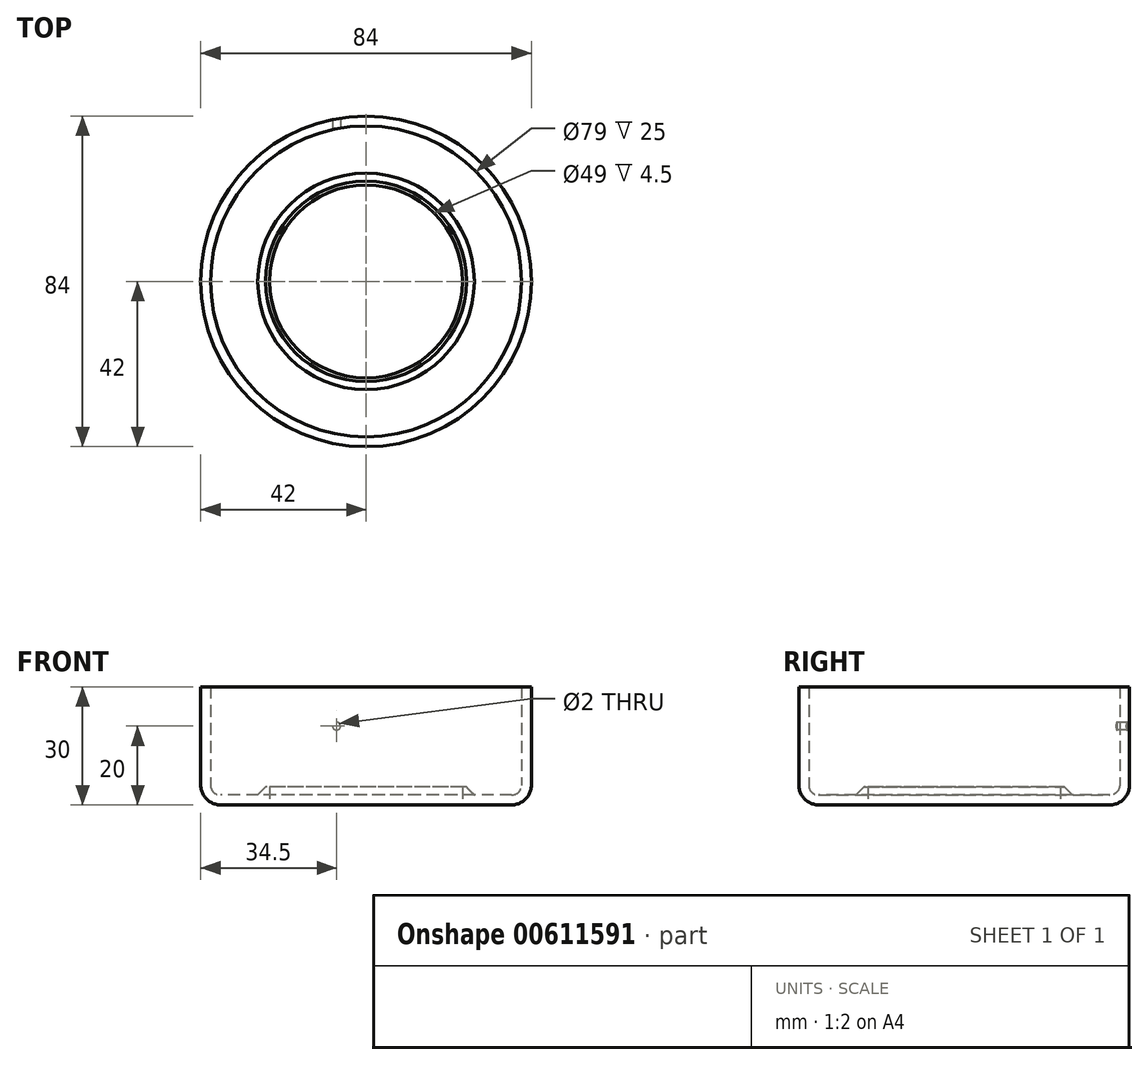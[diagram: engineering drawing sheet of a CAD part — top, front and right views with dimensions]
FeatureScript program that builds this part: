
annotation { "Feature Type Name" : "Feature", "Feature Type Description" : "" }
export const myFeature = defineFeature(function(context is Context, id is Id, definition is map)
    precondition{}
    {
        {
            var Q0;
            Q0=qCreatedBy(makeId("Top.planeOp"),FACE);
            var sketch = newSketch(context, id + "F0", { "sketchPlane" : qUnion([Q0])});
            skCircle(sketch, "E0", {"center": v(0, 0) * mm, "radius": 24.5 * mm});
            skCircle(sketch, "E1", {"center": v(0, 0) * mm, "radius": 42 * mm});
            skCircle(sketch, "E2", {"center": v(0, 0) * mm, "radius": 25.5 * mm});
            skSolve(sketch);
        }
        {
            var Q0;
            Q0=makeQuery(id+"F0.imprint","IMPRINT",FACE,{"disambiguationData":[TD([[makeQuery(id+"F0.imprint","IMPRINT",EDGE,{"derivedFrom":sQuery(id+"F0.wireOp",EDGE,"E1")}),1.0]])]});
            var Q1;
            Q1=makeQuery(id+"F0.imprint","IMPRINT",FACE,{"disambiguationData":[TD([[makeQuery(id+"F0.imprint","IMPRINT",EDGE,{"derivedFrom":sQuery(id+"F0.wireOp",EDGE,"E0")}),1.0]])]});
            var Q2;
            Q2=makeQuery(id+"F0.imprint","IMPRINT",FACE,{"disambiguationData":[TD([[makeQuery(id+"F0.imprint","IMPRINT",EDGE,{"derivedFrom":sQuery(id+"F0.wireOp",EDGE,"E0")}),-1.0]])]});
            extrude(context, id + "F1", {"entities" : qUnion([Q0, Q1, Q2]), "depth" : 30 * mm, "offsetDistance" : 25 * mm});
        }
        {
            var Q0;
            Q0=makeQuery(id+"F1.opExtrude","CAP_EDGE",EDGE,{"disambiguationData":[OSD([sQuery(id+"F0.wireOp",EDGE,"E1")])],"isStart":true});
            var Q1;
            Q1=makeQuery(id+"F1.opExtrude","CAP_FACE",FACE,{"disambiguationData":[OSD([sQuery(id+"F0.wireOp",EDGE,"E1")])],"isStart":true});
            fillet(context, id + "F2", {"entities" : qUnion([Q0, Q1]), "radius" : 5 * mm, "tangentPropagation" : true, "allowEdgeOverflow" : false});
        }
        {
            var Q0;
            Q0=makeQuery(id+"F1.opExtrude","CAP_FACE",FACE,{"disambiguationData":[OSD([sQuery(id+"F0.wireOp",EDGE,"E1")])],"isStart":false});
            shell(context, id + "F3", {"entities" : qUnion([Q0]), "thickness" : 2.5 * mm});
        }
        {
            var Q0;
            Q0=qCreatedBy(makeId("Front.planeOp"),FACE);
            var sketch = newSketch(context, id + "F4", { "sketchPlane" : qUnion([Q0])});
            skCircle(sketch, "E3", {"center": v(-7.5, 20) * mm, "radius": 1 * mm});
            skLineSegment(sketch, "E4", {"start": v(0, 0) * mm, "end": v(0, 66.85) * mm, "construction": true});
            skCircle(sketch, "E5.MirrorC", {"center": v(7.5, 20) * mm, "radius": 1 * mm});
            skSolve(sketch);
        }
        {
            var Q0;
            Q0=makeQuery(id+"F4.imprint","IMPRINT",FACE,{"disambiguationData":[TD([[makeQuery(id+"F4.imprint","IMPRINT",EDGE,{"derivedFrom":sQuery(id+"F4.wireOp",EDGE,"E3")}),1.0]])]});
            var Q1;
            Q1=makeQuery(id+"F4.imprint","IMPRINT",FACE,{"disambiguationData":[TD([[makeQuery(id+"F4.imprint","IMPRINT",EDGE,{"derivedFrom":sQuery(id+"F4.wireOp",EDGE,"E5.MirrorC")}),-1.0]])]});
            extrude(context, id + "F5", {"entities" : qUnion([Q0, Q1]), "operationType" : NewBodyOperationType.REMOVE, "oppositeDirection" : true, "depth" : 100 * mm, "offsetDistance" : 25 * mm});
        }
        {
            var Q0;
            Q0=makeQuery(id+"F0.imprint","IMPRINT",FACE,{"disambiguationData":[TD([[makeQuery(id+"F0.imprint","IMPRINT",EDGE,{"derivedFrom":sQuery(id+"F0.wireOp",EDGE,"E0")}),1.0]])]});
            extrude(context, id + "F6", {"entities" : qUnion([Q0]), "operationType" : NewBodyOperationType.REMOVE, "depth" : 25 * mm, "offsetDistance" : 25 * mm});
        }
        {
            var Q0;
            Q0=makeQuery(id+"F0.imprint","IMPRINT",FACE,{"disambiguationData":[TD([[makeQuery(id+"F0.imprint","IMPRINT",EDGE,{"derivedFrom":sQuery(id+"F0.wireOp",EDGE,"E0")}),-1.0]])]});
            extrude(context, id + "F7", {"entities" : qUnion([Q0]), "operationType" : NewBodyOperationType.ADD, "depth" : 4.5 * mm, "offsetDistance" : 25 * mm});
        }
        {
            var Q0;
            {var subQ0=sQuery(id+"F0.wireOp",EDGE,"E1");Q0=makeQuery(id+"F7.boolean.opBoolean","INTERSECT",EDGE,{"derivedFrom":[makeQuery(id+"F3.opShell","OFFSET_FACE",FACE,{"disambiguationData":[OSD([subQ0]),TDD([makeQuery(id+"F1.opExtrude","CAP_FACE",FACE,{"disambiguationData":[OSD([subQ0])],"isStart":true})])]}),makeQuery(id+"F7.opExtrude","SWEPT_FACE",FACE,{"disambiguationData":[OSD([sQuery(id+"F0.wireOp",EDGE,"E2")])]})]});}
            chamfer(context, id + "F8", {"entities" : qUnion([Q0]), "width" : 2 * mm, "tangentPropagation" : true});
        }
        {
            var Q0;
            Q0=qCreatedBy(makeId("Front.planeOp"),FACE);
            var sketch = newSketch(context, id + "F9", { "sketchPlane" : qUnion([Q0])});
            skLineSegment(sketch, "E6", {"start": v(42, 30) * mm, "end": v(42, 5) * mm});
            skLineSegment(sketch, "E7", {"start": v(-42, 5) * mm, "end": v(-42, 30) * mm});
            skLineSegment(sketch, "E8", {"start": v(39.5, 30) * mm, "end": v(39.5, 5) * mm});
            skLineSegment(sketch, "E9", {"start": v(-39.5, 5) * mm, "end": v(-39.5, 30) * mm});
            skLineSegment(sketch, "E10", {"start": v(-39.5, 30) * mm, "end": v(-42, 30) * mm});
            skLineSegment(sketch, "E11", {"start": v(42, 30) * mm, "end": v(39.5, 30) * mm});
            skLineSegment(sketch, "E12", {"start": v(39.5, 5) * mm, "end": v(42, 5) * mm});
            skLineSegment(sketch, "E13", {"start": v(0, 0) * mm, "end": v(0, 60.3) * mm, "construction": true});
            skLineSegment(sketch, "E14", {"start": v(-42, 5) * mm, "end": v(-39.5, 5) * mm});
            skSolve(sketch);
        }
        {
            var Q0;
            Q0 = qSketchRegion(id + "F9", true);
            var Q1;
            {var subQ0=sQuery(id+"F0.wireOp",EDGE,"E1");Q1=makeQuery(id+"F3.opShell","OFFSET_EDGE",EDGE,{"disambiguationData":[OSD([subQ0]),TDD([makeQuery(id+"F1.opExtrude","CAP_EDGE",EDGE,{"disambiguationData":[OSD([subQ0])],"isStart":false})])]});}
            revolve(context, id + "F10", {"operationType" : NewBodyOperationType.ADD, "surfaceOperationType" : NewSurfaceOperationType.NEW, "entities" : qUnion([Q0]), "axis" : qUnion([Q1]), "revolveType" : RevolveType.ONE_DIRECTION, "angle" : 68.18 * degree});
        }
    });
